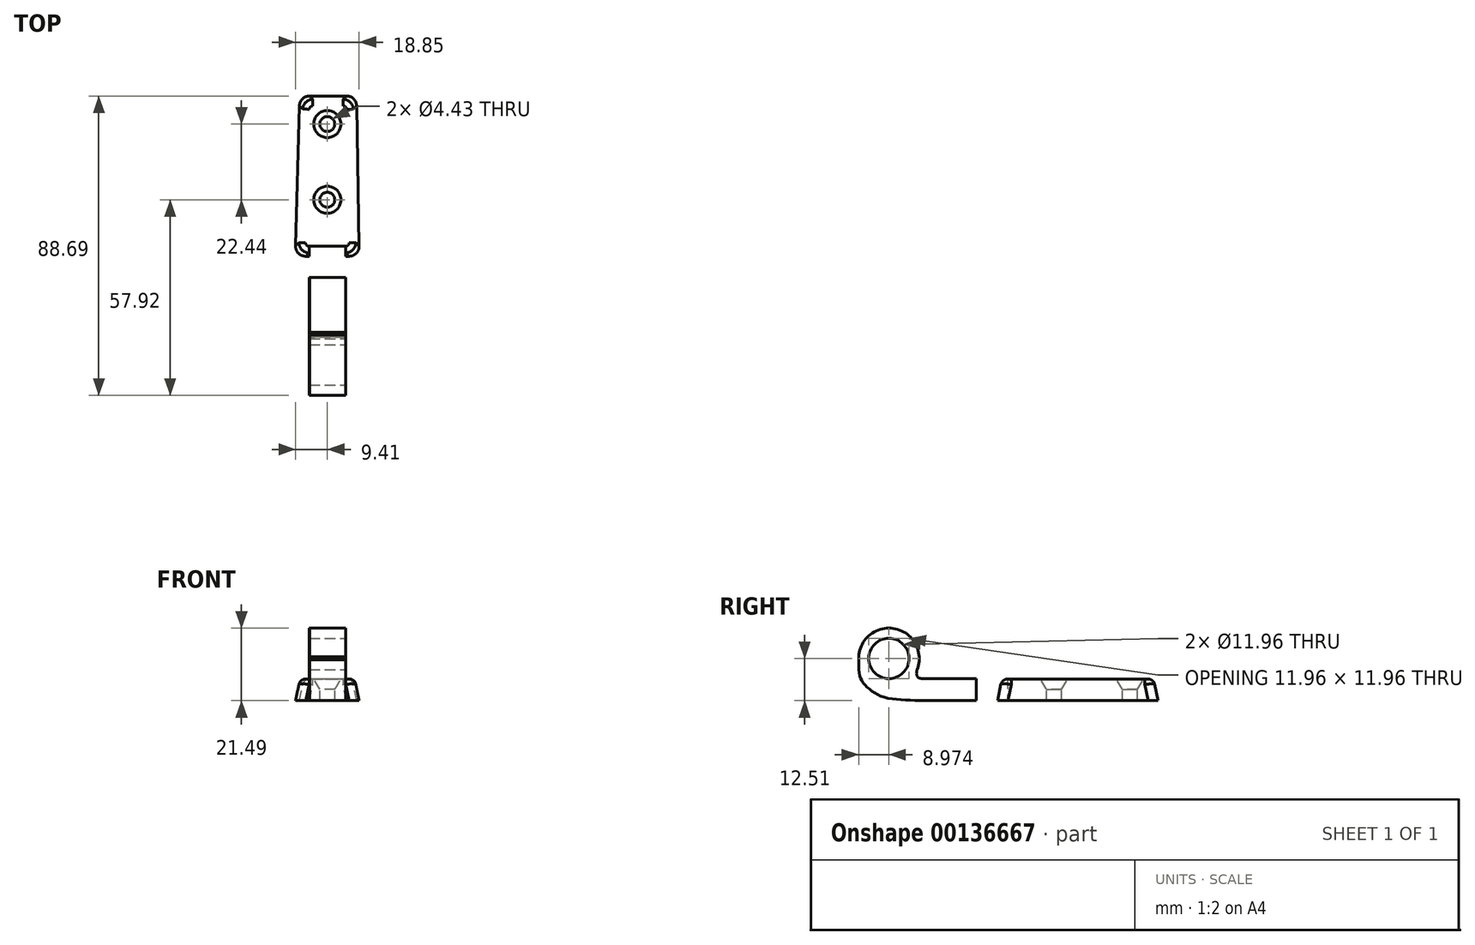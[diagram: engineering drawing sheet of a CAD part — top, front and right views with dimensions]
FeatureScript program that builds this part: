
annotation { "Feature Type Name" : "Feature", "Feature Type Description" : "" }
export const myFeature = defineFeature(function(context is Context, id is Id, definition is map)
    precondition{}
    {
        {
            var Q0;
            Q0=qCreatedBy(makeId("Top.planeOp"),FACE);
            var sketch = newSketch(context, id + "F0", { "sketchPlane" : qUnion([Q0])});
            skLineSegment(sketch, "E0", {"start": v(-5.25, 47.5) * mm, "end": v(5.69, 47.5) * mm});
            skLineSegment(sketch, "E1", {"start": v(-6.41, 0) * mm, "end": v(6.44, 0) * mm});
            skPoint(sketch, "E2", {"position": v(0, 0) * mm});
            skLineSegment(sketch, "E3", {"start": v(0, 47.5) * mm, "end": v(0, 0) * mm, "construction": true});
            skLineSegment(sketch, "E4", {"start": v(-8.25, 44.58) * mm, "end": v(-9.41, 3.08) * mm});
            skLineSegment(sketch, "E5", {"start": v(8.69, 44.55) * mm, "end": v(9.44, 3.05) * mm});
            skPoint(sketch, "E6.visualSharp", {"position": v(-8.17, 47.5) * mm});
            skArc(sketch, "E6.filletArc", {"start": v(-5.25, 47.5) * mm, "mid": v(-7.34, 46.65) * mm, "end": v(-8.25, 44.58) * mm});
            skPoint(sketch, "E7.visualSharp", {"position": v(-9.5, 0) * mm});
            skArc(sketch, "E7.filletArc", {"start": v(-9.41, 3.08) * mm, "mid": v(-8.57, 0.9) * mm, "end": v(-6.41, 0) * mm});
            skPoint(sketch, "E8.visualSharp", {"position": v(9.5, 0) * mm});
            skArc(sketch, "E8.filletArc", {"start": v(6.44, 0) * mm, "mid": v(8.59, 0.9) * mm, "end": v(9.44, 3.05) * mm});
            skPoint(sketch, "E9.visualSharp", {"position": v(8.63, 47.5) * mm});
            skArc(sketch, "E9.filletArc", {"start": v(8.69, 44.55) * mm, "mid": v(7.8, 46.64) * mm, "end": v(5.69, 47.5) * mm});
            skPoint(sketch, "E10", {"position": v(0, 39.17) * mm});
            skPoint(sketch, "E11", {"position": v(0, 16.73) * mm});
            skSolve(sketch);
        }
        {
            var Q0;
            Q0=makeQuery(id+"F0.imprint","IMPRINT",FACE,{"disambiguationData":[TD([[makeQuery(id+"F0.imprint","IMPRINT",EDGE,{"derivedFrom":sQuery(id+"F0.wireOp",EDGE,"E0")}),-1.0]])]});
            cPlane(context, id + "F1", {"entities" : qUnion([Q0]), "cplaneType" : CPlaneType.OFFSET, "offset" : 6.43 * mm, "width" : 150 * mm, "height" : 150 * mm});
        }
        {
            var Q0;
            Q0=qCreatedBy(id+"F1.planeOp",FACE);
            var sketch = newSketch(context, id + "F2", { "sketchPlane" : qUnion([Q0])});
            skLineSegment(sketch, "E12.0", {"start": v(4.41, 46.2) * mm, "end": v(-3.99, 46.2) * mm});
            skLineSegment(sketch, "E12.1", {"start": v(8.12, 4.35) * mm, "end": v(7.41, 43.25) * mm});
            skLineSegment(sketch, "E12.2", {"start": v(-5.08, 1.3) * mm, "end": v(5.12, 1.3) * mm});
            skLineSegment(sketch, "E12.3", {"start": v(-6.98, 43.28) * mm, "end": v(-8.08, 4.38) * mm});
            skPoint(sketch, "E13.visualSharp", {"position": v(7.36, 46.2) * mm});
            skArc(sketch, "E13.filletArc", {"start": v(7.41, 43.25) * mm, "mid": v(6.51, 45.34) * mm, "end": v(4.41, 46.2) * mm});
            skPoint(sketch, "E14.visualSharp", {"position": v(-6.9, 46.2) * mm});
            skArc(sketch, "E14.filletArc", {"start": v(-3.99, 46.2) * mm, "mid": v(-6.08, 45.35) * mm, "end": v(-6.98, 43.28) * mm});
            skPoint(sketch, "E15.visualSharp", {"position": v(8.18, 1.3) * mm});
            skArc(sketch, "E15.filletArc", {"start": v(5.12, 1.3) * mm, "mid": v(7.26, 2.2) * mm, "end": v(8.12, 4.35) * mm});
            skPoint(sketch, "E16.visualSharp", {"position": v(-8.16, 1.3) * mm});
            skArc(sketch, "E16.filletArc", {"start": v(-8.08, 4.38) * mm, "mid": v(-7.23, 2.2) * mm, "end": v(-5.08, 1.3) * mm});
            skPoint(sketch, "E17.0.1.start.orphan", {"position": v(-5.25, 47.5) * mm});
            skPoint(sketch, "E17.0.2.start.orphan", {"position": v(-8.25, 44.58) * mm});
            skPoint(sketch, "E17.0.3.start.orphan", {"position": v(-9.41, 3.08) * mm});
            skPoint(sketch, "E17.0.4.start.orphan", {"position": v(-6.41, 0) * mm});
            skPoint(sketch, "E17.0.5.start.orphan", {"position": v(6.44, 0) * mm});
            skPoint(sketch, "E17.0.6.start.orphan", {"position": v(9.44, 3.05) * mm});
            skPoint(sketch, "E17.0.7.end.orphan", {"position": v(5.69, 47.5) * mm});
            skPoint(sketch, "E17.0.7.start.orphan", {"position": v(8.69, 44.55) * mm});
            skSolve(sketch);
        }
        {
            var Q0;
            Q0=makeQuery(id+"F0.imprint","IMPRINT",FACE,{"disambiguationData":[TD([[makeQuery(id+"F0.imprint","IMPRINT",EDGE,{"derivedFrom":sQuery(id+"F0.wireOp",EDGE,"E0")}),-1.0]])]});
            var Q1;
            Q1=makeQuery(id+"F2.imprint","IMPRINT",FACE,{"disambiguationData":[TD([[makeQuery(id+"F2.imprint","IMPRINT",EDGE,{"derivedFrom":sQuery(id+"F2.wireOp",EDGE,"E12.0")}),1.0]])]});
            loft(context, id + "F3", {"sheetProfilesArray" : [{ "sheetProfileEntities" : qUnion([Q0]) }, { "sheetProfileEntities" : qUnion([Q1]) }]});
        }
        {
            var Q0;
            Q0=makeQuery(id+"F3.opLoft","MID_CAP_EDGE",EDGE,{"disambiguationData":[OSD([sQuery(id+"F2.wireOp",EDGE,"E12.3"),sQuery(id+"F2.wireOp",EDGE,"E14.filletArc"),sQuery(id+"F2.wireOp",EDGE,"E16.filletArc")])],"capPos":1.0});
            var Q1;
            Q1=makeQuery(id+"F3.opLoft","MID_CAP_EDGE",EDGE,{"disambiguationData":[OSD([sQuery(id+"F2.wireOp",EDGE,"E12.0"),sQuery(id+"F2.wireOp",EDGE,"E12.3"),sQuery(id+"F2.wireOp",EDGE,"E14.filletArc")])],"capPos":1.0});
            var Q2;
            Q2=makeQuery(id+"F3.opLoft","MID_CAP_EDGE",EDGE,{"disambiguationData":[OSD([sQuery(id+"F2.wireOp",EDGE,"E12.0"),sQuery(id+"F2.wireOp",EDGE,"E13.filletArc"),sQuery(id+"F2.wireOp",EDGE,"E14.filletArc")])],"capPos":1.0});
            var Q3;
            Q3=makeQuery(id+"F3.opLoft","MID_CAP_EDGE",EDGE,{"disambiguationData":[OSD([sQuery(id+"F2.wireOp",EDGE,"E12.0"),sQuery(id+"F2.wireOp",EDGE,"E12.1"),sQuery(id+"F2.wireOp",EDGE,"E13.filletArc")])],"capPos":1.0});
            var Q4;
            Q4=makeQuery(id+"F3.opLoft","MID_CAP_EDGE",EDGE,{"disambiguationData":[OSD([sQuery(id+"F2.wireOp",EDGE,"E12.1"),sQuery(id+"F2.wireOp",EDGE,"E13.filletArc"),sQuery(id+"F2.wireOp",EDGE,"E15.filletArc")])],"capPos":1.0});
            var Q5;
            Q5=makeQuery(id+"F3.opLoft","MID_CAP_EDGE",EDGE,{"disambiguationData":[OSD([sQuery(id+"F2.wireOp",EDGE,"E12.2"),sQuery(id+"F2.wireOp",EDGE,"E12.3"),sQuery(id+"F2.wireOp",EDGE,"E16.filletArc")])],"capPos":1.0});
            var Q6;
            Q6=makeQuery(id+"F3.opLoft","MID_CAP_EDGE",EDGE,{"disambiguationData":[OSD([sQuery(id+"F2.wireOp",EDGE,"E12.1"),sQuery(id+"F2.wireOp",EDGE,"E12.2"),sQuery(id+"F2.wireOp",EDGE,"E15.filletArc")])],"capPos":1.0});
            fillet(context, id + "F4", {"entities" : qUnion([Q0, Q1, Q2, Q3, Q4, Q5, Q6]), "radius" : 2 * mm, "tangentPropagation" : true, "allowEdgeOverflow" : false});
        }
        {
            var Q0;
            Q0=qCreatedBy(makeId("Right.planeOp"),FACE);
            var sketch = newSketch(context, id + "F5", { "sketchPlane" : qUnion([Q0])});
            skPoint(sketch, "E18", {"position": v(16.73, 0) * mm});
            skPoint(sketch, "E19", {"position": v(39.17, 0) * mm});
            skFitSpline(sketch, "E20.0.2", {"points": [v(4, 6.43) * mm, v(4, 6.43) * mm, v(4, 6.35) * mm, v(4.02, 5.9) * mm, v(4.03, 5.27) * mm, v(4.03, 4.83) * mm]});
            skLineSegment(sketch, "E21", {"start": v(43.2, 6.43) * mm, "end": v(41.39, 3.3) * mm});
            skLineSegment(sketch, "E22", {"start": v(41.39, 3.3) * mm, "end": v(41.39, 0) * mm});
            skLineSegment(sketch, "E23", {"start": v(39.17, 6.43) * mm, "end": v(43.2, 6.43) * mm});
            skLineSegment(sketch, "E24", {"start": v(39.17, 0) * mm, "end": v(39.17, 6.43) * mm});
            skLineSegment(sketch, "E25", {"start": v(41.39, 3.3) * mm, "end": v(41.39, 6.43) * mm, "construction": true});
            skLineSegment(sketch, "E26", {"start": v(41.39, 0) * mm, "end": v(41.39, -1.6) * mm});
            skLineSegment(sketch, "E27", {"start": v(41.39, -1.6) * mm, "end": v(39.29, -1.6) * mm});
            skLineSegment(sketch, "E28", {"start": v(39.29, -1.6) * mm, "end": v(39.17, 0) * mm});
            skLineSegment(sketch, "E29", {"start": v(20.76, 6.43) * mm, "end": v(18.95, 3.3) * mm});
            skLineSegment(sketch, "E30", {"start": v(18.95, 3.3) * mm, "end": v(18.95, 0) * mm});
            skLineSegment(sketch, "E31", {"start": v(16.73, 6.43) * mm, "end": v(20.76, 6.43) * mm});
            skLineSegment(sketch, "E32", {"start": v(16.73, 0) * mm, "end": v(16.73, 6.43) * mm});
            skLineSegment(sketch, "E33", {"start": v(18.95, 0) * mm, "end": v(18.95, -1.6) * mm});
            skLineSegment(sketch, "E34", {"start": v(18.95, -1.6) * mm, "end": v(16.85, -1.6) * mm});
            skLineSegment(sketch, "E35", {"start": v(16.85, -1.6) * mm, "end": v(16.73, 0) * mm});
            skSolve(sketch);
        }
        {
            var Q0;
            Q0=makeQuery(id+"F5.imprint","IMPRINT",FACE,{"disambiguationData":[TD([[makeQuery(id+"F5.imprint","IMPRINT",EDGE,{"derivedFrom":sQuery(id+"F5.wireOp",EDGE,"E21")}),-1.0]])]});
            var Q1;
            Q1=sQuery(id+"F5.wireOp",EDGE,"E24");
            revolve(context, id + "F6", {"operationType" : NewBodyOperationType.REMOVE, "entities" : qUnion([Q0]), "axis" : qUnion([Q1]), "revolveType" : RevolveType.FULL, "oppositeDirection" : true});
        }
        {
            var Q0;
            Q0=makeQuery(id+"F5.imprint","IMPRINT",FACE,{"disambiguationData":[TD([[makeQuery(id+"F5.imprint","IMPRINT",EDGE,{"derivedFrom":sQuery(id+"F5.wireOp",EDGE,"E29")}),-1.0]])]});
            var Q1;
            Q1=sQuery(id+"F5.wireOp",EDGE,"E32");
            revolve(context, id + "F7", {"operationType" : NewBodyOperationType.REMOVE, "entities" : qUnion([Q0]), "axis" : qUnion([Q1]), "revolveType" : RevolveType.FULL, "oppositeDirection" : true});
        }
        {
            var Q0;
            Q0=qCreatedBy(makeId("Front.planeOp"),FACE);
            var Q1;
            {var subQ0=sQuery(id+"F2.wireOp",EDGE,"E12.3");var subQ1=sQuery(id+"F2.wireOp",EDGE,"E12.2");var subQ2=sQuery(id+"F2.wireOp",EDGE,"E15.filletArc");var subQ3=sQuery(id+"F2.wireOp",EDGE,"E16.filletArc");Q1=makeQuery(id+"F4.opFillet","BLEND_VERTEX",VERTEX,{"blendedFrom":[makeQuery(id+"F3.opLoft","MID_CAP_EDGE",EDGE,{"disambiguationData":[OSD([subQ1,subQ2,subQ3])],"capPos":1.0}),makeQuery(id+"F3.opLoft","MID_CAP_EDGE",EDGE,{"disambiguationData":[OSD([subQ1,subQ0,subQ3])],"capPos":1.0}),makeQuery(id+"F3.opLoft","CAP_FACE",FACE,{"disambiguationData":[OSD([makeQuery(id+"F2.imprint","IMPRINT",FACE,{"disambiguationData":[TD([[makeQuery(id+"F2.imprint","IMPRINT",EDGE,{"derivedFrom":sQuery(id+"F2.wireOp",EDGE,"E12.0")}),1.0]])]})])],"isStart":true})],"blendedInto":[makeQuery(id+"F3.opLoft","CAP_FACE",FACE,{"disambiguationData":[OSD([makeQuery(id+"F2.imprint","IMPRINT",FACE,{"disambiguationData":[TD([[makeQuery(id+"F2.imprint","IMPRINT",EDGE,{"derivedFrom":sQuery(id+"F2.wireOp",EDGE,"E12.0")}),1.0]])]})])],"isStart":true})]});}
            cPlane(context, id + "F8", {"entities" : qUnion([Q0, Q1]), "cplaneType" : CPlaneType.PLANE_POINT, "offset" : 25 * mm, "width" : 150 * mm, "height" : 150 * mm});
        }
        {
            var Q0;
            Q0=qCreatedBy(id+"F8.planeOp",FACE);
            var sketch = newSketch(context, id + "F9", { "sketchPlane" : qUnion([Q0])});
            skLineSegment(sketch, "E36.0", {"start": v(-5.41, 6.43) * mm, "end": v(5.45, 6.43) * mm});
            skLineSegment(sketch, "E37", {"start": v(-5.41, 6.43) * mm, "end": v(-5.41, 0) * mm});
            skLineSegment(sketch, "E38", {"start": v(5.45, 6.43) * mm, "end": v(5.45, 0) * mm});
            skLineSegment(sketch, "E39", {"start": v(5.45, 0) * mm, "end": v(-5.41, 0) * mm});
            skSolve(sketch);
        }
        {
            var Q0;
            Q0=qCreatedBy(id+"F8.planeOp",FACE);
            cPlane(context, id + "F10", {"entities" : qUnion([Q0]), "cplaneType" : CPlaneType.OFFSET, "offset" : 25 * mm, "width" : 150 * mm, "height" : 150 * mm});
        }
        {
            var Q0;
            Q0 = qSketchRegion(id + "F9", true);
            var Q1;
            Q1=qCreatedBy(id+"F10.planeOp",FACE);
            extrude(context, id + "F11", {"entities" : qUnion([Q0]), "operationType" : NewBodyOperationType.REMOVE, "endBound" : BoundingType.UP_TO_SURFACE, "endBoundEntityFace" : qUnion([Q1]), "depth" : 25 * mm});
        }
        {
            var Q0;
            Q0=makeQuery(id+"F11.boolean.opBoolean","COPY",FACE,{"derivedFrom":makeQuery(id+"F11.opExtrude","SWEPT_FACE",FACE,{"disambiguationData":[OSD([sQuery(id+"F9.wireOp",EDGE,"E38")])]})});
            cPlane(context, id + "F12", {"entities" : qUnion([Q0]), "cplaneType" : CPlaneType.OFFSET, "offset" : 0 * mm, "width" : 150 * mm, "height" : 150 * mm});
        }
        {
            var Q0;
            Q0=qCreatedBy(id+"F12.planeOp",FACE);
            var sketch = newSketch(context, id + "F13", { "sketchPlane" : qUnion([Q0])});
            skLineSegment(sketch, "E40.0", {"start": v(6.3, 6.53) * mm, "end": v(6.3, 0.1) * mm});
            skLineSegment(sketch, "E41", {"start": v(6.3, 0.1) * mm, "end": v(32.29, 0.1) * mm});
            skLineSegment(sketch, "E42", {"start": v(6.3, 6.53) * mm, "end": v(22.56, 6.53) * mm});
            skPoint(sketch, "E43", {"position": v(32.22, 6.53) * mm});
            skPoint(sketch, "E44", {"position": v(32.22, 12.61) * mm});
            skCircle(sketch, "E45", {"center": v(32.22, 12.51) * mm, "radius": 5.98 * mm});
            skArc(sketch, "E46.0", {"start": v(41.19, 12.16) * mm, "mid": v(30.72, 21.36) * mm, "end": v(23.86, 9.23) * mm});
            skLineSegment(sketch, "E47", {"start": v(41.19, 12.16) * mm, "end": v(41.18, 13.02) * mm});
            skLineSegment(sketch, "E48.trimOffspring", {"start": v(41.24, 6.53) * mm, "end": v(41.3, 6.53) * mm});
            skPoint(sketch, "E49.visualSharp", {"position": v(41.3, 0.1) * mm});
            skPoint(sketch, "E50", {"position": v(24.49, 0.1) * mm});
            skFitSpline(sketch, "E51", {"points": [v(41.19, 12.16) * mm, v(40.83, 7.22) * mm, v(38.68, 4.03) * mm, v(34, 1.14) * mm, v(24.49, 0.1) * mm], "startDerivative": vector(-0.05, -22.3) * mm, "endDerivative": vector(-32.04, -1.25) * mm});
            skFitSpline(sketch, "E52", {"points": [v(23.86, 9.23) * mm, v(24.04, 7.92) * mm, v(23.65, 6.98) * mm, v(22.56, 6.53) * mm], "startDerivative": vector(0.84, -3.78) * mm, "endDerivative": vector(-3.71, -0.94) * mm});
            skSolve(sketch);
        }
        {
            var Q0;
            Q0=makeQuery(id+"F13.imprint","IMPRINT",FACE,{"disambiguationData":[TD([[makeQuery(id+"F13.imprint","IMPRINT",EDGE,{"derivedFrom":sQuery(id+"F13.wireOp",EDGE,"E40.0")}),1.0]])]});
            var Q1;
            Q1=makeQuery(id+"F11.boolean.opBoolean","COPY",FACE,{"derivedFrom":makeQuery(id+"F11.opExtrude","SWEPT_FACE",FACE,{"disambiguationData":[OSD([sQuery(id+"F9.wireOp",EDGE,"E37")])]})});
            extrude(context, id + "F14", {"entities" : qUnion([Q0]), "operationType" : NewBodyOperationType.ADD, "endBound" : BoundingType.UP_TO_SURFACE, "endBoundEntityFace" : qUnion([Q1]), "depth" : 25 * mm});
        }
        {
            var Q0;
            Q0=makeQuery(id+"F11.boolean.opBoolean","COPY",FACE,{"derivedFrom":makeQuery(id+"F11.opExtrude","SWEPT_FACE",FACE,{"disambiguationData":[OSD([sQuery(id+"F9.wireOp",EDGE,"E37")])]})});
            cPlane(context, id + "F15", {"entities" : qUnion([Q0]), "cplaneType" : CPlaneType.OFFSET, "offset" : .2 * mm, "width" : 150 * mm, "height" : 150 * mm});
        }
        {
            var Q0;
            Q0=makeQuery(id+"F13.imprint","IMPRINT",FACE,{"disambiguationData":[TD([[makeQuery(id+"F13.imprint","IMPRINT",EDGE,{"derivedFrom":sQuery(id+"F13.wireOp",EDGE,"E40.0")}),1.0]])]});
            var Q1;
            Q1=qCreatedBy(id+"F15.planeOp",FACE);
            extrude(context, id + "F16", {"entities" : qUnion([Q0]), "endBound" : BoundingType.UP_TO_SURFACE, "endBoundEntityFace" : qUnion([Q1]), "depth" : 25 * mm});
        }
        {
            var Q0;
            Q0=makeQuery(id+"F3.opLoft","SWEPT_BODY",BODY,{"disambiguationData":[OSD([makeQuery(id+"F0.imprint","IMPRINT",FACE,{"disambiguationData":[TD([[makeQuery(id+"F0.imprint","IMPRINT",EDGE,{"derivedFrom":sQuery(id+"F0.wireOp",EDGE,"E0")}),-1.0]])]}),makeQuery(id+"F2.imprint","IMPRINT",FACE,{"disambiguationData":[TD([[makeQuery(id+"F2.imprint","IMPRINT",EDGE,{"derivedFrom":sQuery(id+"F2.wireOp",EDGE,"E12.0")}),1.0]])]})])]});
            transform(context, id + "F17", {"entities" : qUnion([Q0]), "transformType" : TransformType.TRANSLATION_3D, "dx" : 0 * mm, "dy" : -192.97 * mm, "dz" : 0 * mm, "makeCopy" : true});
        }
        {
            var Q0;
            Q0=makeQuery(id+"F17.opPattern","COPY",BODY,{"derivedFrom":makeQuery(id+"F3.opLoft","SWEPT_BODY",BODY,{"disambiguationData":[OSD([makeQuery(id+"F0.imprint","IMPRINT",FACE,{"disambiguationData":[TD([[makeQuery(id+"F0.imprint","IMPRINT",EDGE,{"derivedFrom":sQuery(id+"F0.wireOp",EDGE,"E0")}),-1.0]])]}),makeQuery(id+"F2.imprint","IMPRINT",FACE,{"disambiguationData":[TD([[makeQuery(id+"F2.imprint","IMPRINT",EDGE,{"derivedFrom":sQuery(id+"F2.wireOp",EDGE,"E12.0")}),1.0]])]})])]}),"instanceName":"1"});
            deleteBodies(context, id + "F18", {"entities" : qUnion([Q0])});
        }
    });
